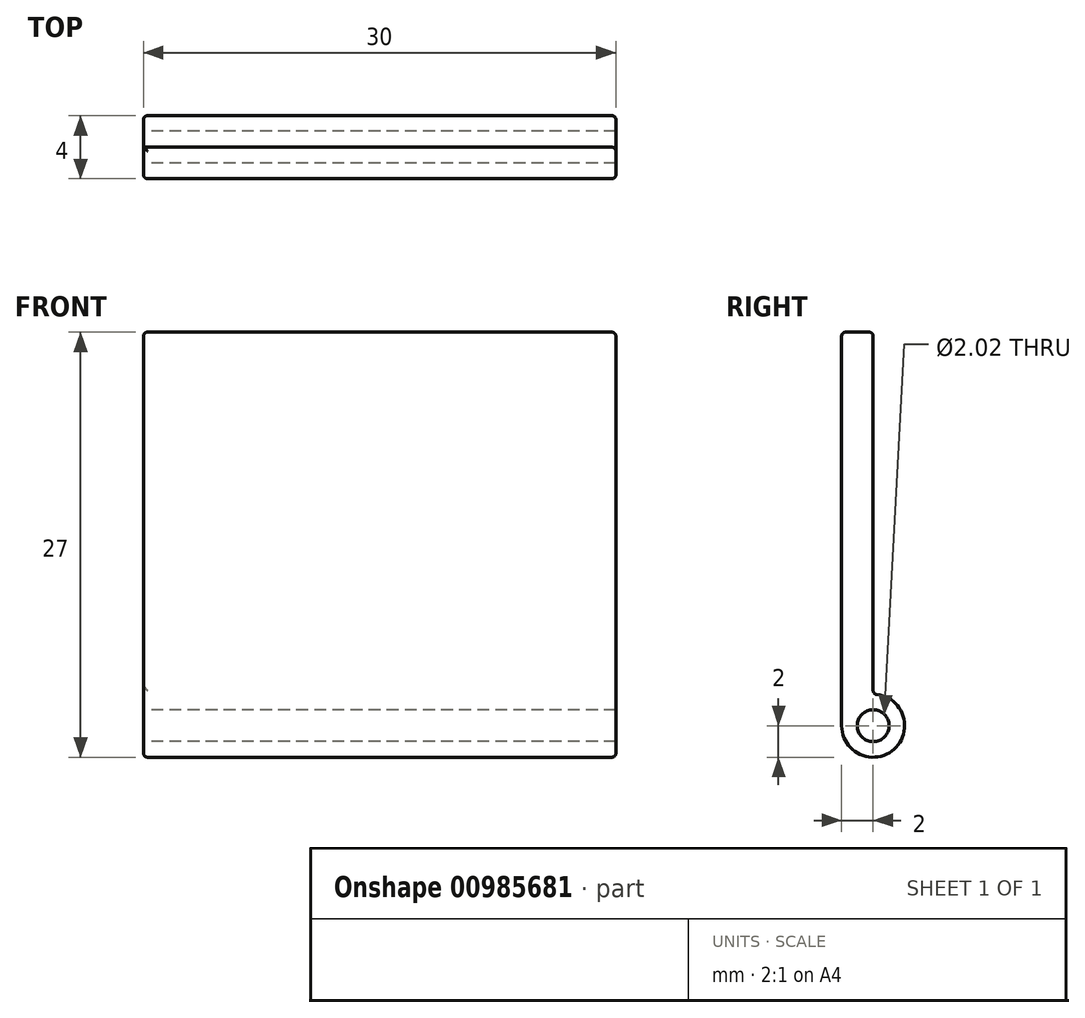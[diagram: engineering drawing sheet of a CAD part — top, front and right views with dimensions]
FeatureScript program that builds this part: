
annotation { "Feature Type Name" : "Feature", "Feature Type Description" : "" }
export const myFeature = defineFeature(function(context is Context, id is Id, definition is map)
    precondition{}
    {
        {
            assignVariable(context, id + "F0", {"name" : "wd", "anyValue" : 30});
        }
        {
            var Q0;
            Q0=qCreatedBy(makeId("Right.planeOp"),FACE);
            var sketch = newSketch(context, id + "F1", { "sketchPlane" : qUnion([Q0])});
            skLineSegment(sketch, "E0", {"start": v(0, 0) * mm, "end": v(0, 25) * mm});
            skLineSegment(sketch, "E1", {"start": v(0, 25) * mm, "end": v(2, 25) * mm});
            skLineSegment(sketch, "E2", {"start": v(2, 25) * mm, "end": v(2, 2) * mm});
            skLineSegment(sketch, "E3", {"start": v(0.99, 0) * mm, "end": v(0, 0) * mm});
            skArc(sketch, "E4", {"start": v(0, 0) * mm, "mid": v(3.41, -1.41) * mm, "end": v(2, 2) * mm});
            skPoint(sketch, "E4.second.point", {"position": v(4, 0) * mm});
            skLineSegment(sketch, "E5", {"start": v(1, 0) * mm, "end": v(4, 0) * mm, "construction": true});
            skCircle(sketch, "E6", {"center": v(2, 0) * mm, "radius": 1.01 * mm});
            skLineSegment(sketch, "E7", {"start": v(2, 2) * mm, "end": v(2, 0) * mm, "construction": true});
            skSolve(sketch);
        }
        {
            var Q0;
            Q0=makeQuery(id+"F1.imprint","IMPRINT",FACE,{"disambiguationData":[TD([[makeQuery(id+"F1.imprint","IMPRINT",EDGE,{"derivedFrom":sQuery(id+"F1.wireOp",EDGE,"E0")}),-1.0]])]});
            extrude(context, id + "F2", {"entities" : qUnion([Q0]), "depth" : (getVariable(context, 'wd')) * mm, "offsetDistance" : 25 * mm});
        }
        {
            var Q0;
            Q0=makeQuery(id+"F2.opExtrude","CAP_EDGE",EDGE,{"disambiguationData":[OSD([sQuery(id+"F1.wireOp",EDGE,"E2")])],"isStart":false});
            var Q1;
            Q1=makeQuery(id+"F2.opExtrude","CAP_EDGE",EDGE,{"disambiguationData":[OSD([sQuery(id+"F1.wireOp",EDGE,"E0")])],"isStart":false});
            var Q2;
            Q2=makeQuery(id+"F2.opExtrude","SWEPT_EDGE",EDGE,{"disambiguationData":[OSD([sQuery(id+"F1.wireOp",EDGE,"E2"),sQuery(id+"F1.wireOp",EDGE,"E4")])]});
            var Q3;
            Q3=makeQuery(id+"F2.opExtrude","CAP_EDGE",EDGE,{"disambiguationData":[OSD([sQuery(id+"F1.wireOp",EDGE,"E0")])],"isStart":true});
            var Q4;
            Q4=makeQuery(id+"F2.opExtrude","SWEPT_EDGE",EDGE,{"disambiguationData":[OSD([sQuery(id+"F1.wireOp",EDGE,"E1"),sQuery(id+"F1.wireOp",EDGE,"E2")])]});
            var Q5;
            Q5=makeQuery(id+"F2.opExtrude","SWEPT_EDGE",EDGE,{"disambiguationData":[OSD([sQuery(id+"F1.wireOp",EDGE,"E0"),sQuery(id+"F1.wireOp",EDGE,"E1")])]});
            var Q6;
            Q6=makeQuery(id+"F2.opExtrude","CAP_EDGE",EDGE,{"disambiguationData":[OSD([sQuery(id+"F1.wireOp",EDGE,"E1")])],"isStart":true});
            var Q7;
            Q7=makeQuery(id+"F2.opExtrude","CAP_EDGE",EDGE,{"disambiguationData":[OSD([sQuery(id+"F1.wireOp",EDGE,"E1")])],"isStart":false});
            fillet(context, id + "F3", {"entities" : qUnion([Q0, Q1, Q2, Q3, Q4, Q5, Q6, Q7]), "radius" : .25 * mm, "tangentPropagation" : true, "allowEdgeOverflow" : false});
        }
    });
